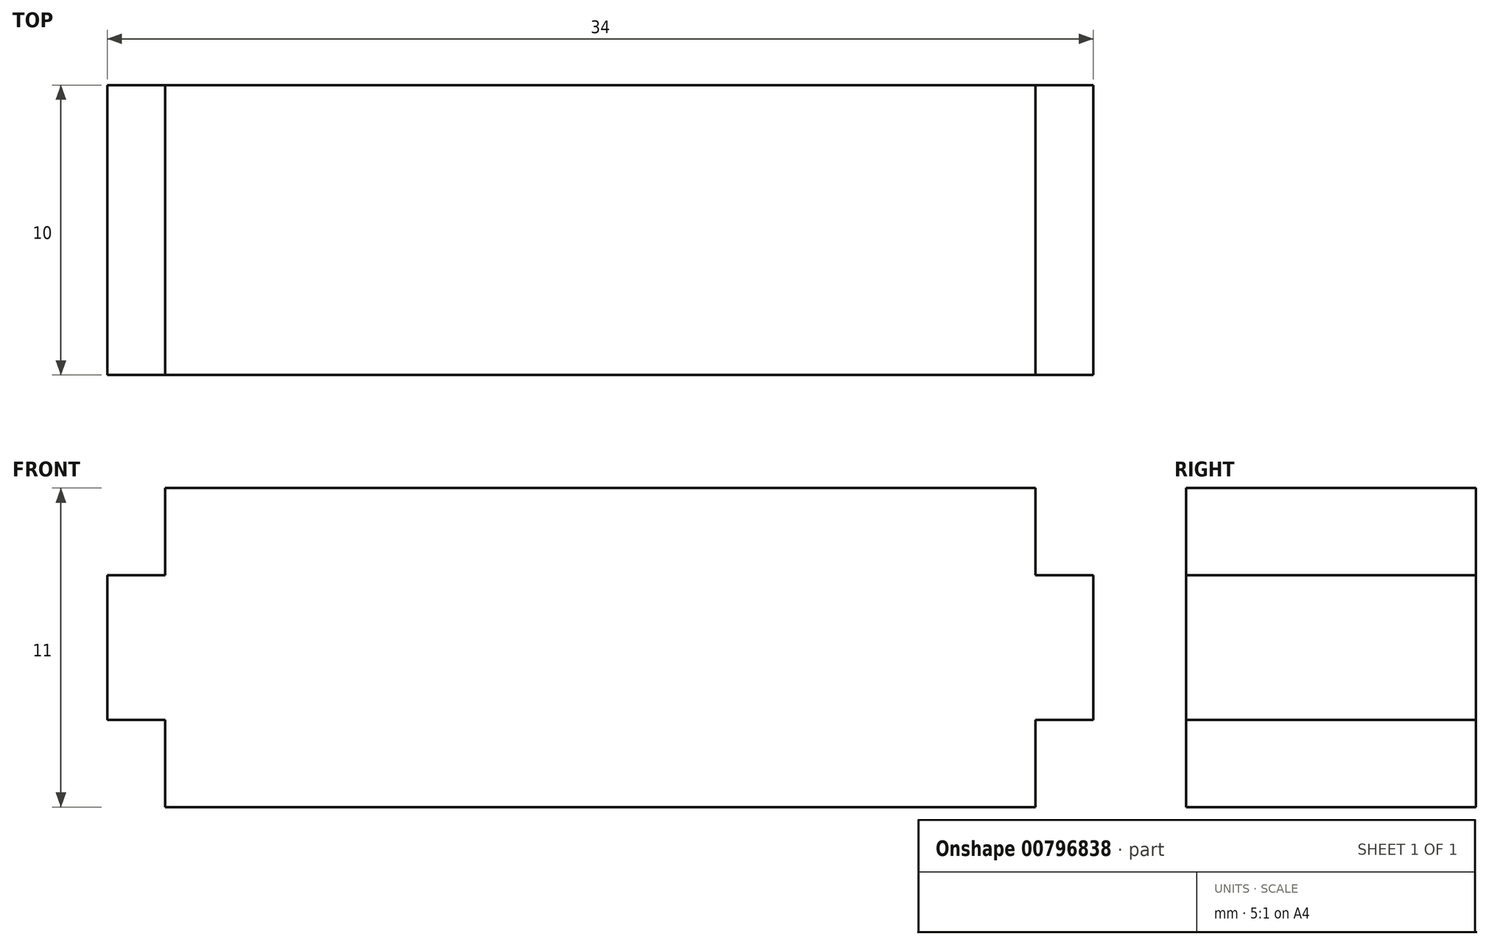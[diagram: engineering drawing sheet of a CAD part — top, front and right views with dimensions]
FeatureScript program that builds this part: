
annotation { "Feature Type Name" : "Feature", "Feature Type Description" : "" }
export const myFeature = defineFeature(function(context is Context, id is Id, definition is map)
    precondition{}
    {
        {
            var Q0;
            Q0=qCreatedBy(makeId("Top.planeOp"),FACE);
            var sketch = newSketch(context, id + "F0", { "sketchPlane" : qUnion([Q0])});
            skLineSegment(sketch, "E0.bottom", {"start": v(15, -5) * mm, "end": v(-15, -5) * mm});
            skLineSegment(sketch, "E0.top", {"start": v(15, 5) * mm, "end": v(-15, 5) * mm});
            skLineSegment(sketch, "E0.left", {"start": v(15, -5) * mm, "end": v(15, 5) * mm});
            skLineSegment(sketch, "E0.right", {"start": v(-15, -5) * mm, "end": v(-15, 5) * mm});
            skPoint(sketch, "E0.middle", {"position": v(0, 0) * mm});
            skSolve(sketch);
        }
        {
            var Q0;
            Q0=makeQuery(id+"F0.imprint","IMPRINT",FACE,{"disambiguationData":[TD([[makeQuery(id+"F0.imprint","IMPRINT",EDGE,{"derivedFrom":sQuery(id+"F0.wireOp",EDGE,"E0.bottom")}),-1.0]])]});
            extrude(context, id + "F1", {"entities" : qUnion([Q0]), "depth" : 3 * mm, "offsetDistance" : 25 * mm});
        }
        {
            var Q0;
            Q0=makeQuery(id+"F1.opExtrude","CAP_FACE",FACE,{"disambiguationData":[OSD([sQuery(id+"F0.wireOp",EDGE,"E0.bottom"),sQuery(id+"F0.wireOp",EDGE,"E0.top"),sQuery(id+"F0.wireOp",EDGE,"E0.left"),sQuery(id+"F0.wireOp",EDGE,"E0.right")])],"isStart":false});
            var sketch = newSketch(context, id + "F2", { "sketchPlane" : qUnion([Q0])});
            skLineSegment(sketch, "E1.bottom", {"start": v(17, -5) * mm, "end": v(-17, -5) * mm});
            skLineSegment(sketch, "E1.top", {"start": v(17, 5) * mm, "end": v(-17, 5) * mm});
            skLineSegment(sketch, "E1.left", {"start": v(17, -5) * mm, "end": v(17, 5) * mm});
            skLineSegment(sketch, "E1.right", {"start": v(-17, -5) * mm, "end": v(-17, 5) * mm});
            skPoint(sketch, "E1.middle", {"position": v(0, 0) * mm});
            skSolve(sketch);
        }
        {
            var Q0;
            Q0 = qSketchRegion(id + "F2", true);
            extrude(context, id + "F3", {"entities" : qUnion([Q0]), "operationType" : NewBodyOperationType.ADD, "depth" : 5 * mm, "offsetDistance" : 25 * mm});
        }
        {
            var Q0;
            Q0=makeQuery(id+"F3.opExtrude","CAP_FACE",FACE,{"disambiguationData":[OSD([sQuery(id+"F2.wireOp",EDGE,"E1.bottom"),sQuery(id+"F2.wireOp",EDGE,"E1.top"),sQuery(id+"F2.wireOp",EDGE,"E1.left"),sQuery(id+"F2.wireOp",EDGE,"E1.right")])],"isStart":false});
            var sketch = newSketch(context, id + "F4", { "sketchPlane" : qUnion([Q0])});
            skLineSegment(sketch, "E2.bottom", {"start": v(15, -5) * mm, "end": v(-15, -5) * mm});
            skLineSegment(sketch, "E2.top", {"start": v(15, 5) * mm, "end": v(-15, 5) * mm});
            skLineSegment(sketch, "E2.left", {"start": v(15, -5) * mm, "end": v(15, 5) * mm});
            skLineSegment(sketch, "E2.right", {"start": v(-15, -5) * mm, "end": v(-15, 5) * mm});
            skPoint(sketch, "E2.middle", {"position": v(0, 0) * mm});
            skSolve(sketch);
        }
        {
            var Q0;
            Q0 = qSketchRegion(id + "F4", true);
            extrude(context, id + "F5", {"entities" : qUnion([Q0]), "operationType" : NewBodyOperationType.ADD, "depth" : 2 * mm, "offsetDistance" : 25 * mm});
        }
        {
            var Q0;
            Q0=makeQuery(id+"F5.opExtrude","CAP_FACE",FACE,{"disambiguationData":[OSD([sQuery(id+"F4.wireOp",EDGE,"E2.bottom"),sQuery(id+"F4.wireOp",EDGE,"E2.top"),sQuery(id+"F4.wireOp",EDGE,"E2.left"),sQuery(id+"F4.wireOp",EDGE,"E2.right")])],"isStart":false});
            var sketch = newSketch(context, id + "F6", { "sketchPlane" : qUnion([Q0])});
            skLineSegment(sketch, "E3.bottom", {"start": v(15, -5) * mm, "end": v(-15, -5) * mm});
            skLineSegment(sketch, "E3.top", {"start": v(15, 5) * mm, "end": v(-15, 5) * mm});
            skLineSegment(sketch, "E3.left", {"start": v(15, -5) * mm, "end": v(15, 5) * mm});
            skLineSegment(sketch, "E3.right", {"start": v(-15, -5) * mm, "end": v(-15, 5) * mm});
            skPoint(sketch, "E3.middle", {"position": v(0, 0) * mm});
            skSolve(sketch);
        }
        {
            var Q0;
            Q0 = qSketchRegion(id + "F6", true);
            extrude(context, id + "F7", {"entities" : qUnion([Q0]), "operationType" : NewBodyOperationType.ADD, "depth" : 1 * mm, "offsetDistance" : 25 * mm});
        }
    });
